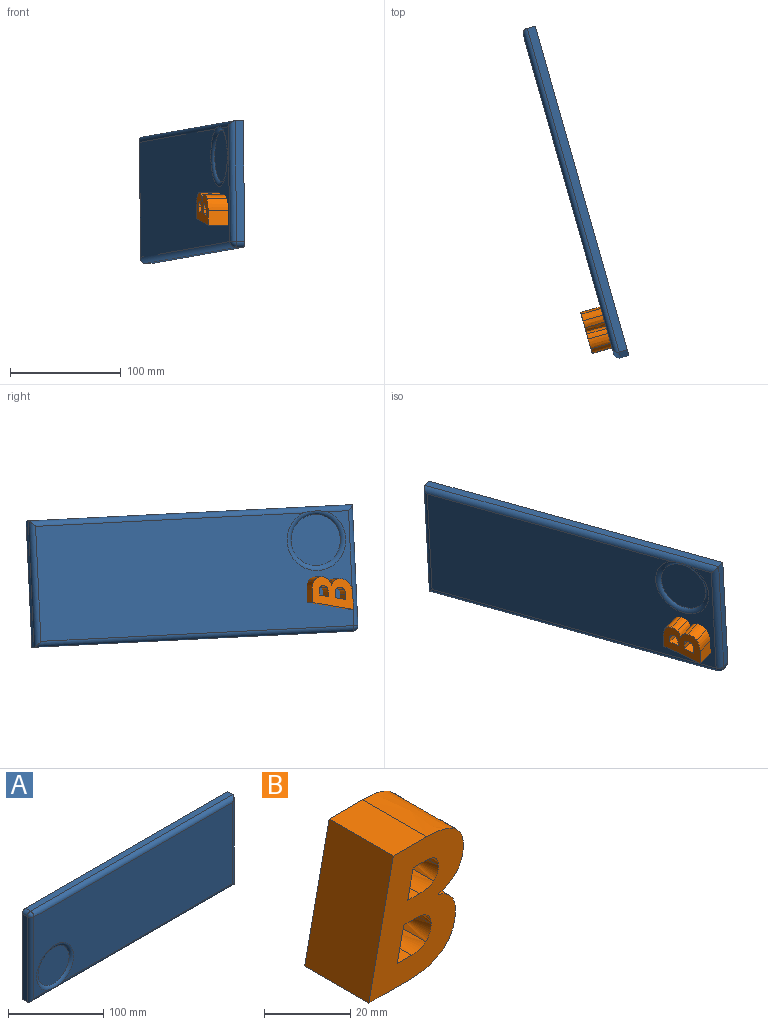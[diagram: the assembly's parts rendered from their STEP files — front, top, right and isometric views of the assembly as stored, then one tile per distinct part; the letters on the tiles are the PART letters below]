
ASSEMBLY  parts=2 mates=1
PART A: 14 faces, bbox 304.8x12.7x117.9 mm
  f0: plane 114.3x7.62mm, normal (1,0,0), area 871mm2, adj f1,f3,f5,f10
  f1: plane 299.72x7.62mm, normal (0,0,1), area 2283.9mm2, adj f0,f5,f7,f8
  f2: plane 109.22x7.62mm, normal (-1,0,0), area 832.3mm2, adj f3,f5,f7,f11
  f3: plane 304.8x7.62mm, normal (0,0,-1), area 2322.6mm2, adj f0,f2,f5,f12
  f4: plane 294.64x104.14mm, normal (0,-1,0), area 28332.2mm2, adj f8,f10,f11,f12,f13
  f5: plane 304.8x114.3mm, normal (0,1,0), area 34833.1mm2, adj f0,f1,f2,f3,f7
  f6: plane 46.36x46.36mm, normal (0,-1,0), area 1687.9mm2, adj f13
  f7: cylinder r=5.08mm len=7.62mm, axis (0,1,0), area 60.8mm2, adj f1,f2,f5,f9
  f8: cylinder r=5.08mm len=299.72mm, axis (1,0,0), area 2376.9mm2, adj f1,f4,f9,f10
  f9: sphere r=5.08mm, area 40.5mm2, adj f7,f8,f11
  f10: cylinder r=5.08mm len=114.3mm, axis (0,0,-1), area 882.6mm2, adj f0,f4,f8,f12
  f11: cylinder r=5.08mm len=109.22mm, axis (0,0,1), area 856.8mm2, adj f2,f4,f9,f12
  f12: cylinder r=5.08mm len=304.8mm, axis (-1,0,0), area 2383.9mm2, adj f3,f4,f10,f11,f13
  f13: torus R=27.58mm, axis (0,-1,0), area 821.5mm2, adj f4,f6,f12
PART B: 26 faces, bbox 30.9x21.1x37.8 mm
  f0: plane 21.08x4.65mm, normal (0,0,1), area 98mm2, adj f1,f23,f24,f25
  f1: plane 21.08x9.85mm, normal (0.98,0,-0.21), area 212.4mm2, adj f0,f2,f24,f25
  f2: plane 21.08x4.26mm, normal (0,0,-1), area 89.8mm2, adj f1,f3,f24,f25
  f3: extruded ~21.08x4.73mm, area 152.8mm2, adj f2,f4,f24,f25
  f4: extruded ~21.08x4.15mm, area 97.9mm2, adj f3,f23,f24,f25
  f5: plane 21.08x3.85mm, normal (0,0,1), area 81.2mm2, adj f6,f21,f24,f25
  f6: plane 21.08x8.4mm, normal (0.98,0,-0.21), area 181.1mm2, adj f5,f7,f24,f25
  f7: plane 21.08x3.93mm, normal (0,0,-1), area 82.8mm2, adj f6,f8,f24,f25
  f8: extruded ~21.08x4.39mm, area 136mm2, adj f7,f9,f24,f25
  f9: extruded ~21.08x3.61mm, area 85.9mm2, adj f8,f21,f24,f25
  f10: extruded ~21.08x8.93mm, area 196.4mm2, adj f11,f22,f24,f25
  f11: plane 21.08x11.01mm, normal (0,0,1), area 232.2mm2, adj f10,f12,f24,f25
  f12: plane 37.78x21.08mm, normal (-0.98,0,0.21), area 814.1mm2, adj f11,f13,f24,f25
  f13: plane 21.08x13.49mm, normal (0,0,-1), area 284.3mm2, adj f12,f14,f24,f25
  f14: extruded ~21.08x10.93mm, area 244.9mm2, adj f13,f15,f24,f25
  f15: extruded ~21.08x9.12mm, area 217.3mm2, adj f14,f16,f24,f25
  f16: extruded ~21.08x4.66mm, area 105.7mm2, adj f15,f17,f24,f25
  f17: extruded ~21.08x4.12mm, area 103.2mm2, adj f16,f18,f24,f25
  f18: plane 21.08x0.16mm, normal (1,0,0), area 3.3mm2, adj f17,f19,f24,f25
  f19: extruded ~21.08x6.09mm, area 149.3mm2, adj f18,f20,f24,f25
  f20: extruded ~21.08x6.4mm, area 145.3mm2, adj f19,f22,f24,f25
  f21: extruded ~21.08x4.69mm, area 104.3mm2, adj f5,f9,f24,f25
  f22: extruded ~21.08x6.29mm, area 153.5mm2, adj f10,f20,f24,f25
  f23: extruded ~21.08x4.74mm, area 107.2mm2, adj f0,f4,f24,f25
  f24: plane 37.78x30.95mm, normal (0,-1,0), area 729.9mm2, adj f0,f1,f2,f3,f4,f5,f6,f7
  f25: plane 37.78x30.95mm, normal (0,1,0), area 729.9mm2, adj f0,f1,f2,f3,f4,f5,f6,f7
PLACE A rot(axis=(0.6,0.8,-0.01),177.8deg) t=(-79.48,101.33,-9.47)mm
PLACE B rot(axis=(-0.52,-0.69,-0.5),113.2deg) t=(-51.71,-33.79,94.88)mm
MATE planar A.f13 <-> B.f25  axis (-0.96,-0.27,0) through (-58.01,-11.61,23.05)mm
